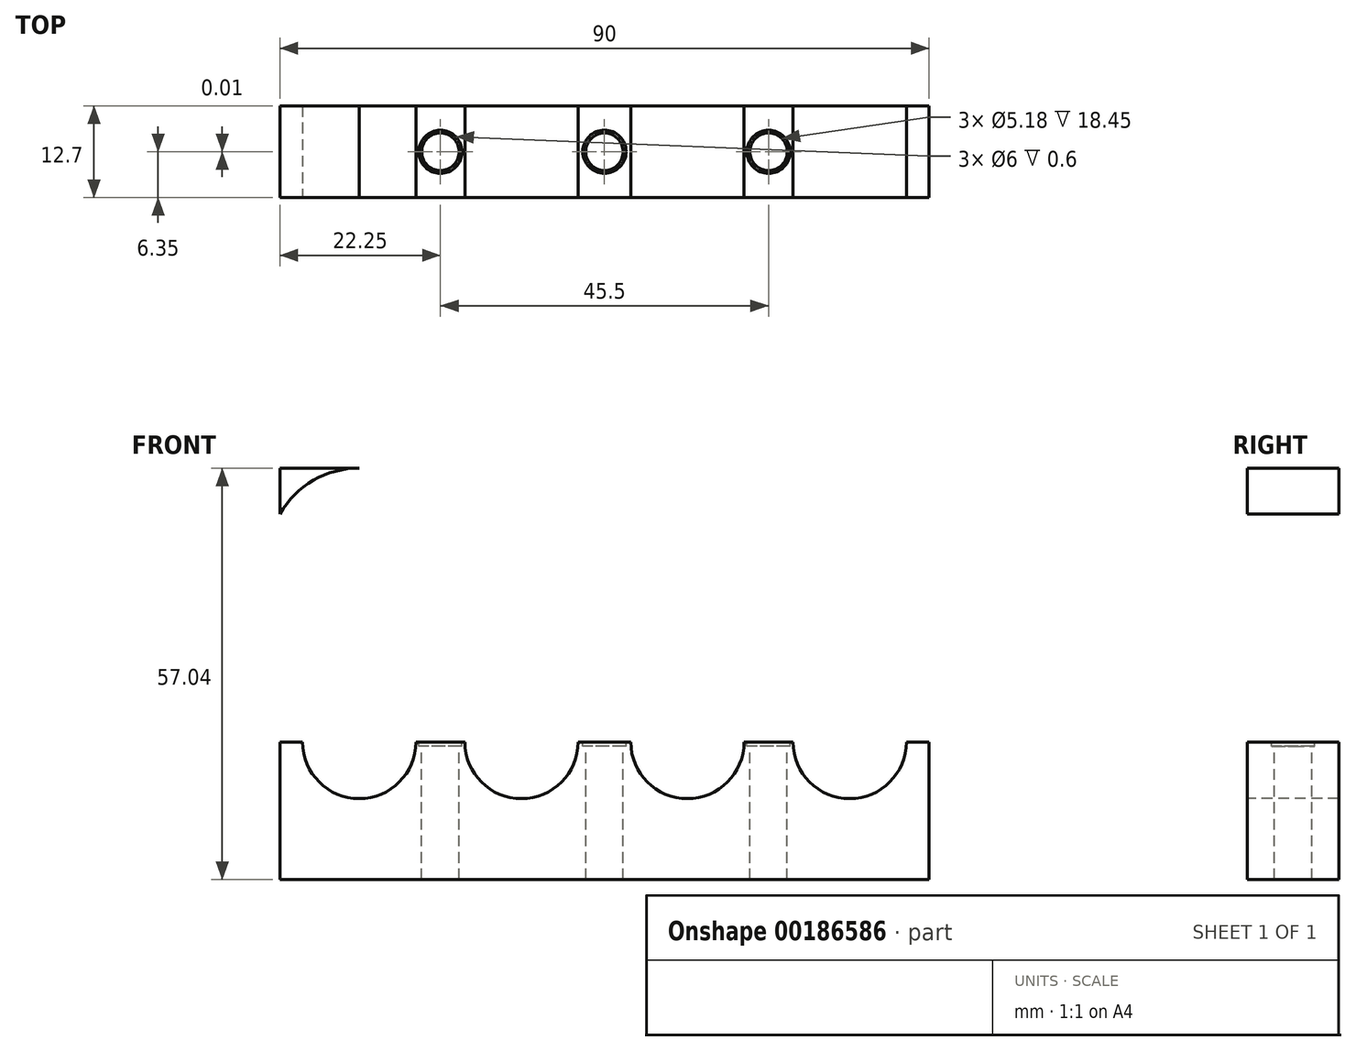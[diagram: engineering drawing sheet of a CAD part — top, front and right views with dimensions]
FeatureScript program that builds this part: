
annotation { "Feature Type Name" : "Feature", "Feature Type Description" : "" }
export const myFeature = defineFeature(function(context is Context, id is Id, definition is map)
    precondition{}
    {
        {
            var Q0;
            Q0=qCreatedBy(makeId("Front.planeOp"),FACE);
            var sketch = newSketch(context, id + "F0", { "sketchPlane" : qUnion([Q0])});
            skLineSegment(sketch, "E0.bottom", {"start": v(45, 9.52) * mm, "end": v(-45, 9.53) * mm});
            skLineSegment(sketch, "E0.top", {"start": v(45, -9.53) * mm, "end": v(-45, -9.52) * mm});
            skLineSegment(sketch, "E0.left", {"start": v(45, 9.52) * mm, "end": v(45, -9.53) * mm});
            skLineSegment(sketch, "E0.right", {"start": v(-45, 9.53) * mm, "end": v(-45, -9.52) * mm});
            skPoint(sketch, "E0.middle", {"position": v(0, 0) * mm});
            skSolve(sketch);
        }
        {
            var Q0;
            Q0=qSketchRegion(id+"F0",true);
            extrude(context, id + "F1", {"entities" : qUnion([Q0]), "depth" : 12.7 * mm});
        }
        {
            var Q0;
            Q0=makeQuery(id+"F1.opExtrude","CAP_FACE",FACE,{"disambiguationData":[OSD([sQuery(id+"F0.wireOp",EDGE,"E0.bottom"),sQuery(id+"F0.wireOp",EDGE,"E0.top"),sQuery(id+"F0.wireOp",EDGE,"E0.left"),sQuery(id+"F0.wireOp",EDGE,"E0.right")])],"isStart":false});
            var sketch = newSketch(context, id + "F2", { "sketchPlane" : qUnion([Q0])});
            skCircle(sketch, "E1", {"center": v(-34, 9.52) * mm, "radius": 7.85 * mm});
            skCircle(sketch, "E2", {"center": v(-11.5, 9.52) * mm, "radius": 7.85 * mm});
            skCircle(sketch, "E3.MirrorC", {"center": v(11.5, 9.52) * mm, "radius": 7.85 * mm});
            skCircle(sketch, "E4.MirrorC", {"center": v(34, 9.52) * mm, "radius": 7.85 * mm});
            skSolve(sketch);
        }
        {
            var Q0;
            Q0=qSketchRegion(id+"F2",true);
            extrude(context, id + "F3", {"entities" : qUnion([Q0]), "operationType" : NewBodyOperationType.REMOVE, "oppositeDirection" : true, "depth" : 25.4 * mm});
        }
        {
            var Q0;
            Q0=qCreatedBy(makeId("Front.planeOp"),FACE);
            var sketch = newSketch(context, id + "F4", { "sketchPlane" : qUnion([Q0])});
            skLineSegment(sketch, "E5.bottom", {"start": v(45, 34.81) * mm, "end": v(-45, 34.81) * mm});
            skLineSegment(sketch, "E5.top", {"start": v(45, 47.51) * mm, "end": v(-45, 47.51) * mm});
            skLineSegment(sketch, "E5.left", {"start": v(45, 34.81) * mm, "end": v(45, 47.51) * mm});
            skLineSegment(sketch, "E5.right", {"start": v(-45, 34.81) * mm, "end": v(-45, 47.51) * mm});
            skPoint(sketch, "E5.middle", {"position": v(0, 41.16) * mm});
            skSolve(sketch);
        }
        {
            var Q0;
            Q0=makeQuery(id+"F4.imprint","IMPRINT",FACE,{"disambiguationData":[TD([[makeQuery(id+"F4.imprint","IMPRINT",EDGE,{"derivedFrom":sQuery(id+"F4.wireOp",EDGE,"E5.bottom")}),-1.0]])]});
            extrude(context, id + "F5", {"entities" : qUnion([Q0]), "depth" : 12.7 * mm});
        }
        {
            var Q0;
            Q0=makeQuery(id+"F5.opExtrude","CAP_FACE",FACE,{"disambiguationData":[OSD([sQuery(id+"F4.wireOp",EDGE,"E5.bottom"),sQuery(id+"F4.wireOp",EDGE,"E5.top"),sQuery(id+"F4.wireOp",EDGE,"E5.left"),sQuery(id+"F4.wireOp",EDGE,"E5.right")])],"isStart":false});
            var sketch = newSketch(context, id + "F6", { "sketchPlane" : qUnion([Q0])});
            skCircle(sketch, "E6", {"center": v(-34, 34.81) * mm, "radius": 7.85 * mm});
            skCircle(sketch, "E7", {"center": v(-11.5, 34.81) * mm, "radius": 7.85 * mm});
            skCircle(sketch, "E8.MirrorC", {"center": v(11.5, 34.81) * mm, "radius": 7.85 * mm});
            skCircle(sketch, "E9.MirrorC", {"center": v(34, 34.81) * mm, "radius": 7.85 * mm});
            skSolve(sketch);
        }
        {
            var Q0;
            Q0=qSketchRegion(id+"F6",true);
            extrude(context, id + "F7", {"entities" : qUnion([Q0]), "operationType" : NewBodyOperationType.REMOVE, "oppositeDirection" : true, "depth" : 25.4 * mm});
        }
        {
            var Q0;
            Q0=makeQuery(id+"F5.opExtrude","SWEPT_FACE",FACE,{"disambiguationData":[OSD([sQuery(id+"F4.wireOp",EDGE,"E5.top")])]});
            var sketch = newSketch(context, id + "F8", { "sketchPlane" : qUnion([Q0])});
            skCircle(sketch, "E10", {"center": v(-22.75, -6.35) * mm, "radius": 2.25 * mm});
            skCircle(sketch, "E11", {"center": v(0, -6.35) * mm, "radius": 2.25 * mm});
            skCircle(sketch, "E12", {"center": v(22.75, -6.35) * mm, "radius": 2.25 * mm});
            skSolve(sketch);
        }
        {
            var Q0;
            Q0=qSketchRegion(id+"F8",true);
            extrude(context, id + "F9", {"entities" : qUnion([Q0]), "operationType" : NewBodyOperationType.REMOVE, "oppositeDirection" : true, "depth" : 25.4 * mm});
        }
        {
            var Q0;
            {var subQ0=sQuery(id+"F0.wireOp",EDGE,"E0.right");var subQ1=sQuery(id+"F0.wireOp",EDGE,"E0.left");var subQ2=sQuery(id+"F0.wireOp",EDGE,"E0.top");var subQ3=sQuery(id+"F0.wireOp",EDGE,"E0.bottom");Q0=makeQuery(id+"F3.boolean.opBoolean","SPLIT",FACE,{"disambiguationData":[TD([makeQuery(id+"F1.opExtrude","CAP_FACE",FACE,{"disambiguationData":[OSD([subQ3,subQ2,subQ1,subQ0])],"isStart":true}),makeQuery(id+"F1.opExtrude","CAP_FACE",FACE,{"disambiguationData":[OSD([subQ3,subQ2,subQ1,subQ0])],"isStart":false}),makeQuery(id+"F3.opExtrude","SWEPT_FACE",FACE,{"disambiguationData":[OSD([sQuery(id+"F2.wireOp",EDGE,"E1")])]}),makeQuery(id+"F3.opExtrude","SWEPT_FACE",FACE,{"disambiguationData":[OSD([sQuery(id+"F2.wireOp",EDGE,"E2")])]})])],"derivedFrom":makeQuery(id+"F1.opExtrude","SWEPT_FACE",FACE,{"disambiguationData":[OSD([subQ3])]})});}
            var sketch = newSketch(context, id + "F10", { "sketchPlane" : qUnion([Q0])});
            skCircle(sketch, "E13", {"center": v(-22.75, -6.35) * mm, "radius": 2.6 * mm});
            skCircle(sketch, "E14", {"center": v(0, -6.35) * mm, "radius": 2.6 * mm});
            skCircle(sketch, "E15", {"center": v(22.75, -6.35) * mm, "radius": 2.6 * mm});
            skSolve(sketch);
        }
        {
            var Q0;
            Q0=qSketchRegion(id+"F10",true);
            extrude(context, id + "F11", {"entities" : qUnion([Q0]), "operationType" : NewBodyOperationType.REMOVE, "oppositeDirection" : true, "depth" : 20 * mm});
        }
        {
            var Q0;
            {var subQ0=sQuery(id+"F0.wireOp",EDGE,"E0.right");var subQ1=sQuery(id+"F0.wireOp",EDGE,"E0.left");var subQ2=sQuery(id+"F0.wireOp",EDGE,"E0.top");var subQ3=sQuery(id+"F0.wireOp",EDGE,"E0.bottom");Q0=makeQuery(id+"F3.boolean.opBoolean","SPLIT",FACE,{"disambiguationData":[TD([makeQuery(id+"F1.opExtrude","CAP_FACE",FACE,{"disambiguationData":[OSD([subQ3,subQ2,subQ1,subQ0])],"isStart":true}),makeQuery(id+"F1.opExtrude","CAP_FACE",FACE,{"disambiguationData":[OSD([subQ3,subQ2,subQ1,subQ0])],"isStart":false}),makeQuery(id+"F3.opExtrude","SWEPT_FACE",FACE,{"disambiguationData":[OSD([sQuery(id+"F2.wireOp",EDGE,"E1")])]}),makeQuery(id+"F3.opExtrude","SWEPT_FACE",FACE,{"disambiguationData":[OSD([sQuery(id+"F2.wireOp",EDGE,"E2")])]})])],"derivedFrom":makeQuery(id+"F1.opExtrude","SWEPT_FACE",FACE,{"disambiguationData":[OSD([subQ3])]})});}
            var sketch = newSketch(context, id + "F12", { "sketchPlane" : qUnion([Q0])});
            skCircle(sketch, "E16", {"center": v(-22.75, -6.35) * mm, "radius": 3 * mm});
            skCircle(sketch, "E17.MirrorC", {"center": v(22.75, -6.35) * mm, "radius": 3 * mm});
            skCircle(sketch, "E18", {"center": v(0, -6.34) * mm, "radius": 3 * mm});
            skSolve(sketch);
        }
        {
            var Q0;
            Q0=qSketchRegion(id+"F12",true);
            extrude(context, id + "F13", {"entities" : qUnion([Q0]), "operationType" : NewBodyOperationType.REMOVE, "oppositeDirection" : true, "depth" : 0.5 * mm});
        }
        {
            var Q0;
            Q0=qSketchRegion(id+"F12",true);
            extrude(context, id + "F14", {"entities" : qUnion([Q0]), "operationType" : NewBodyOperationType.REMOVE, "oppositeDirection" : true, "depth" : 0.6 * mm});
        }
        {
            var Q0;
            Q0=makeQuery(id+"F5.opExtrude","CAP_FACE",FACE,{"disambiguationData":[OSD([sQuery(id+"F4.wireOp",EDGE,"E5.bottom"),sQuery(id+"F4.wireOp",EDGE,"E5.top"),sQuery(id+"F4.wireOp",EDGE,"E5.left"),sQuery(id+"F4.wireOp",EDGE,"E5.right")])],"isStart":true});
            var sketch = newSketch(context, id + "F15", { "sketchPlane" : qUnion([Q0])});
            skLineSegment(sketch, "E19.0", {"start": v(45, 34.81) * mm, "end": v(45, 47.51) * mm});
            skLineSegment(sketch, "E20.0", {"start": v(-45, 47.51) * mm, "end": v(45, 47.51) * mm});
            skLineSegment(sketch, "E21.0", {"start": v(-45, 34.81) * mm, "end": v(-45, 47.51) * mm});
            skArc(sketch, "E22.0", {"start": v(-34, 47.51) * mm, "mid": v(-40.35, 45.81) * mm, "end": v(-45, 41.16) * mm});
            skArc(sketch, "E23.0", {"start": v(34, 47.51) * mm, "mid": v(40.35, 45.81) * mm, "end": v(45, 41.16) * mm});
            skSolve(sketch);
        }
        {
            var Q0;
            {var subQ3=sQuery(id+"F15.wireOp",EDGE,"E23.0");Q0=makeQuery(id+"F15.imprint","IMPRINT",FACE,{"disambiguationData":[TD([[makeQuery(id+"F15.imprint","IMPRINT",EDGE,{"derivedFrom":subQ3}),1.0]])]});}
            var Q1;
            {var subQ3=sQuery(id+"F15.wireOp",EDGE,"E22.0");Q1=makeQuery(id+"F15.imprint","IMPRINT",FACE,{"disambiguationData":[TD([[makeQuery(id+"F15.imprint","IMPRINT",EDGE,{"derivedFrom":subQ3}),-1.0]])]});}
            var Q2;
            Q2=makeQuery(id+"F5.opExtrude","CAP_FACE",FACE,{"disambiguationData":[OSD([sQuery(id+"F4.wireOp",EDGE,"E5.bottom"),sQuery(id+"F4.wireOp",EDGE,"E5.top"),sQuery(id+"F4.wireOp",EDGE,"E5.left"),sQuery(id+"F4.wireOp",EDGE,"E5.right")])],"isStart":false});
            extrude(context, id + "F16", {"entities" : qUnion([Q0, Q1]), "operationType" : NewBodyOperationType.REMOVE, "endBound" : BoundingType.UP_TO_SURFACE, "oppositeDirection" : true, "endBoundEntityFace" : qUnion([Q2]), "depth" : 25 * mm});
        }
    });
